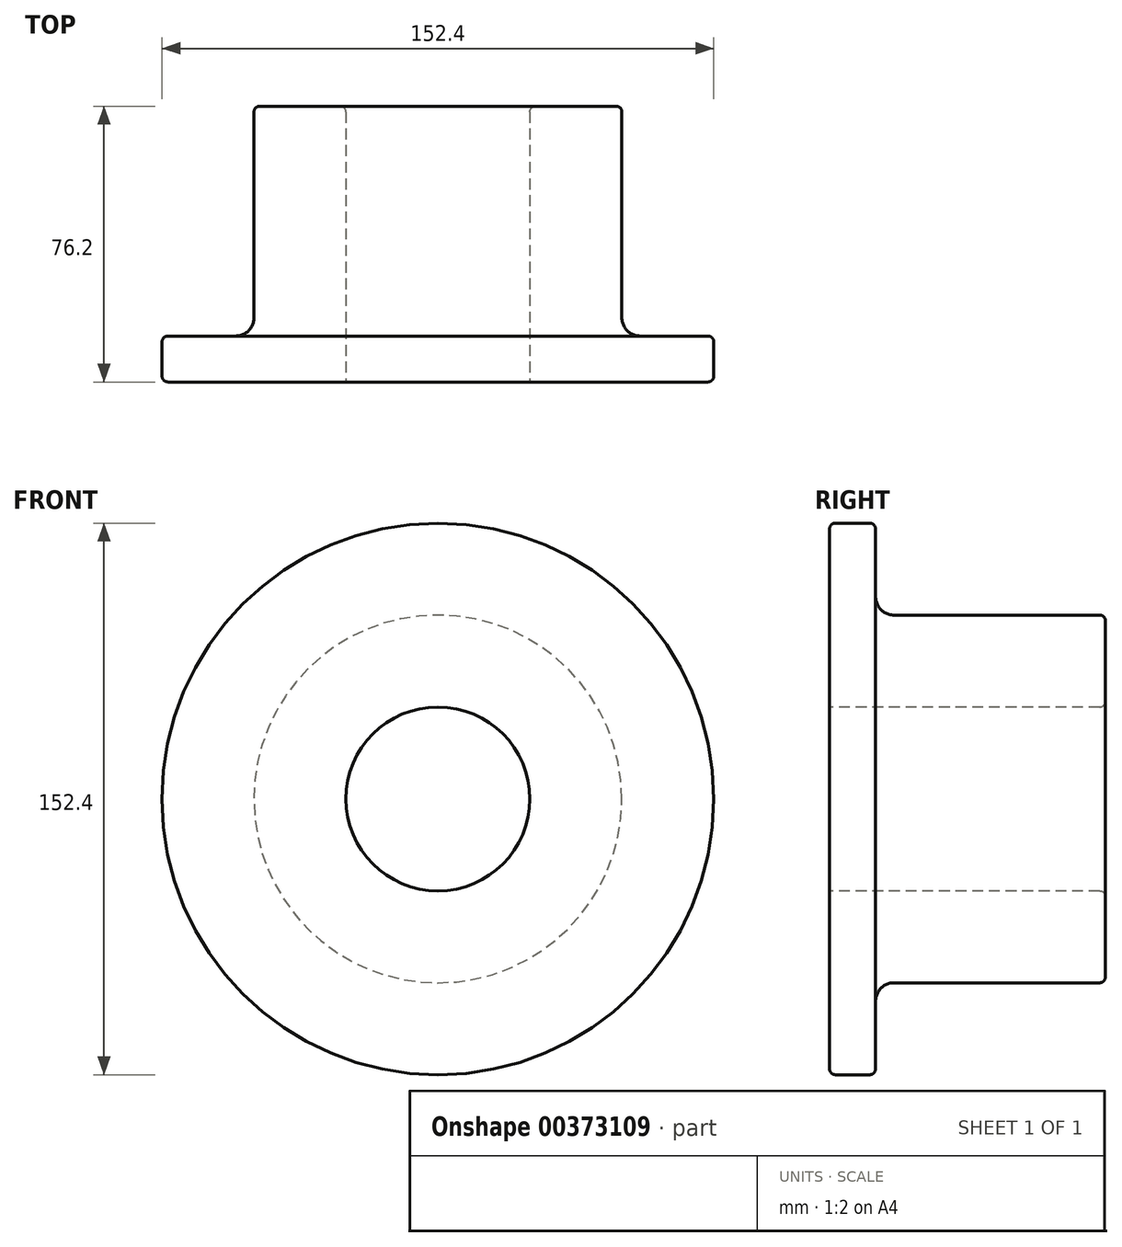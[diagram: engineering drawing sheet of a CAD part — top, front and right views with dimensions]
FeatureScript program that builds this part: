
annotation { "Feature Type Name" : "Feature", "Feature Type Description" : "" }
export const myFeature = defineFeature(function(context is Context, id is Id, definition is map)
    precondition{}
    {
        {
            var Q0;
            Q0=qCreatedBy(makeId("Right.planeOp"),FACE);
            var sketch = newSketch(context, id + "F0", { "sketchPlane" : qUnion([Q0])});
            skLineSegment(sketch, "E0", {"start": v(0, 0) * mm, "end": v(90.52, 0) * mm, "construction": true});
            skLineSegment(sketch, "E1.bottom", {"start": v(0, 25.4) * mm, "end": v(76.2, 25.4) * mm});
            skLineSegment(sketch, "E1.top", {"start": v(0, 50.8) * mm, "end": v(76.2, 50.8) * mm});
            skLineSegment(sketch, "E1.left", {"start": v(0, 25.4) * mm, "end": v(0, 50.8) * mm});
            skLineSegment(sketch, "E1.right", {"start": v(76.2, 25.4) * mm, "end": v(76.2, 50.8) * mm});
            skLineSegment(sketch, "E2.bottom", {"start": v(0, 25.4) * mm, "end": v(12.7, 25.4) * mm});
            skLineSegment(sketch, "E2.top", {"start": v(0, 76.2) * mm, "end": v(12.7, 76.2) * mm});
            skLineSegment(sketch, "E2.left", {"start": v(0, 25.4) * mm, "end": v(0, 76.2) * mm});
            skLineSegment(sketch, "E2.right", {"start": v(12.7, 25.4) * mm, "end": v(12.7, 76.2) * mm});
            skLineSegment(sketch, "E3.left", {"start": v(90.52, 0) * mm, "end": v(90.52, 0) * mm});
            skLineSegment(sketch, "E3.right", {"start": v(76.2, 0) * mm, "end": v(76.2, 0) * mm});
            skLineSegment(sketch, "E4.MirrorCS", {"start": v(0, -25.4) * mm, "end": v(0, -50.8) * mm});
            skLineSegment(sketch, "E5.MirrorCS", {"start": v(0, -50.8) * mm, "end": v(76.2, -50.8) * mm});
            skLineSegment(sketch, "E6.MirrorCS", {"start": v(0, -76.2) * mm, "end": v(12.7, -76.2) * mm});
            skLineSegment(sketch, "E7.MirrorCS", {"start": v(76.2, -25.4) * mm, "end": v(76.2, -50.8) * mm});
            skLineSegment(sketch, "E8.MirrorCS", {"start": v(0, -25.4) * mm, "end": v(12.7, -25.4) * mm});
            skLineSegment(sketch, "E9.MirrorCS", {"start": v(0, -25.4) * mm, "end": v(0, -76.2) * mm});
            skLineSegment(sketch, "E10.MirrorCS", {"start": v(12.7, -25.4) * mm, "end": v(12.7, -76.2) * mm});
            skLineSegment(sketch, "E11.MirrorCS", {"start": v(0, -25.4) * mm, "end": v(76.2, -25.4) * mm});
            skSolve(sketch);
        }
        {
            var Q0;
            {var subQ5=sQuery(id+"F0.wireOp",EDGE,"E2.top");Q0=makeQuery(id+"F0.imprint","IMPRINT",FACE,{"disambiguationData":[TD([[makeQuery(id+"F0.imprint","IMPRINT",EDGE,{"derivedFrom":subQ5}),-1.0]])]});}
            var Q1;
            {var subQ5=sQuery(id+"F0.wireOp",EDGE,"E2.bottom");Q1=makeQuery(id+"F0.imprint","IMPRINT",FACE,{"disambiguationData":[TD([[makeQuery(id+"F0.imprint","IMPRINT",EDGE,{"derivedFrom":subQ5}),1.0]])]});}
            var Q2;
            {var subQ0=sQuery(id+"F0.wireOp",EDGE,"E1.bottom");Q2=makeQuery(id+"F0.imprint","IMPRINT",FACE,{"disambiguationData":[TD([[makeQuery(id+"F0.imprint","IMPRINT",EDGE,{"derivedFrom":subQ0}),1.0]])]});}
            var Q3;
            Q3=sQuery(id+"F0.wireOp",EDGE,"E0");
            revolve(context, id + "F1", {"entities" : qUnion([Q0, Q1, Q2]), "axis" : qUnion([Q3]), "revolveType" : RevolveType.FULL});
        }
        {
            var Q0;
            Q0=makeQuery(id+"F1.opRevolve","SWEPT_EDGE",EDGE,{"disambiguationData":[OSD([sQuery(id+"F0.wireOp",EDGE,"E2.top"),sQuery(id+"F0.wireOp",EDGE,"E2.right")])]});
            var Q1;
            Q1=makeQuery(id+"F1.opRevolve","SWEPT_EDGE",EDGE,{"disambiguationData":[OSD([sQuery(id+"F0.wireOp",EDGE,"E2.top"),sQuery(id+"F0.wireOp",EDGE,"E2.left")])]});
            var Q2;
            Q2=makeQuery(id+"F1.opRevolve","SWEPT_EDGE",EDGE,{"disambiguationData":[OSD([sQuery(id+"F0.wireOp",EDGE,"E1.top"),sQuery(id+"F0.wireOp",EDGE,"E1.right")])]});
            var Q3;
            Q3=makeQuery(id+"F1.opRevolve","SWEPT_EDGE",EDGE,{"disambiguationData":[OSD([sQuery(id+"F0.wireOp",EDGE,"E1.bottom"),sQuery(id+"F0.wireOp",EDGE,"E1.right")])]});
            var Q4;
            Q4=makeQuery(id+"F1.opRevolve","SWEPT_EDGE",EDGE,{"disambiguationData":[OSD([sQuery(id+"F0.wireOp",EDGE,"E2.bottom"),sQuery(id+"F0.wireOp",EDGE,"E2.left")])]});
            fillet(context, id + "F2", {"entities" : qUnion([Q0, Q1, Q2, Q3, Q4]), "radius" : 1.59 * mm, "tangentPropagation" : true, "allowEdgeOverflow" : false});
        }
        {
            var Q0;
            Q0=makeQuery(id+"F1.opRevolve","SWEPT_EDGE",EDGE,{"disambiguationData":[OSD([sQuery(id+"F0.wireOp",EDGE,"E1.top"),sQuery(id+"F0.wireOp",EDGE,"E2.right")])]});
            fillet(context, id + "F3", {"entities" : qUnion([Q0]), "radius" : 5.08 * mm, "tangentPropagation" : true, "allowEdgeOverflow" : false});
        }
    });
